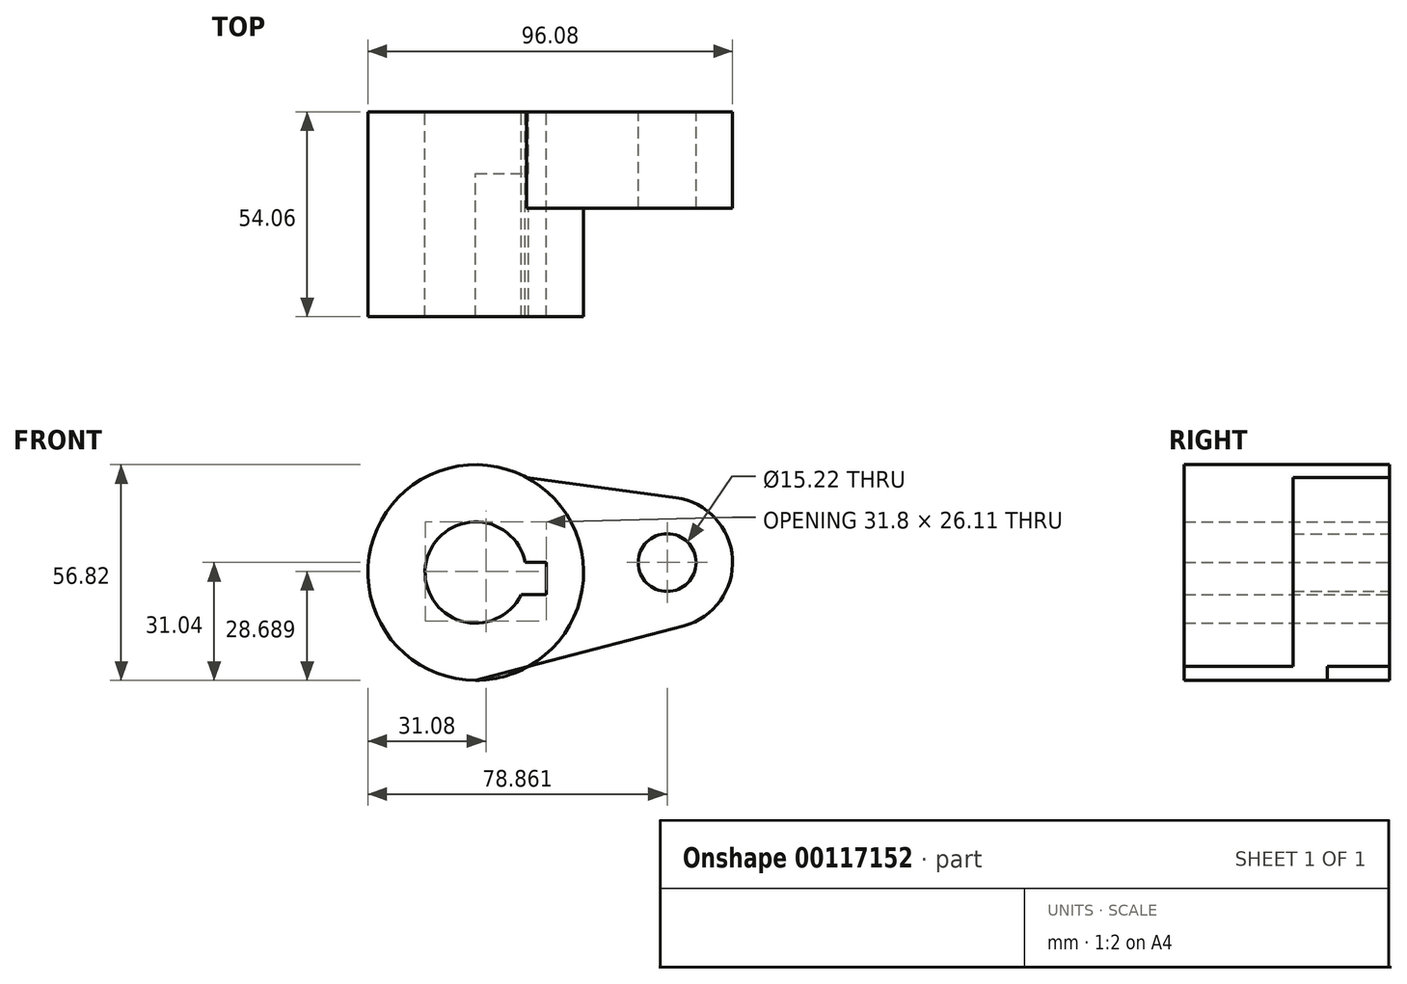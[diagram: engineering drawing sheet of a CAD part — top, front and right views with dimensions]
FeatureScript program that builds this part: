
annotation { "Feature Type Name" : "Feature", "Feature Type Description" : "" }
export const myFeature = defineFeature(function(context is Context, id is Id, definition is map)
    precondition{}
    {
        {
            var Q0;
            Q0=qCreatedBy(makeId("Front.planeOp"),FACE);
            var sketch = newSketch(context, id + "F0", { "sketchPlane" : qUnion([Q0])});
            skCircle(sketch, "E0", {"center": v(0, -2.63) * mm, "radius": 28.4 * mm});
            skCircle(sketch, "E1", {"center": v(50.45, 0) * mm, "radius": 17.22 * mm});
            skLineSegment(sketch, "E2", {"start": v(0, -31.04) * mm, "end": v(54.82, -16.66) * mm});
            skLineSegment(sketch, "E3", {"start": v(13.45, 22.4) * mm, "end": v(52.76, 17.07) * mm});
            skCircle(sketch, "E4", {"center": v(0, -2.63) * mm, "radius": 13.34 * mm});
            skCircle(sketch, "E5", {"center": v(50.45, 0) * mm, "radius": 7.6 * mm});
            skLineSegment(sketch, "E6.bottom", {"start": v(-17.95, 0) * mm, "end": v(18.57, 0) * mm});
            skLineSegment(sketch, "E6.top", {"start": v(-17.95, -8.51) * mm, "end": v(18.57, -8.51) * mm});
            skLineSegment(sketch, "E6.left", {"start": v(-17.95, 0) * mm, "end": v(-17.95, -8.51) * mm});
            skLineSegment(sketch, "E6.right", {"start": v(18.57, 0) * mm, "end": v(18.57, -8.51) * mm});
            skSolve(sketch);
        }
        {
            var Q0;
            {var subQ0=sQuery(id+"F0.wireOp",EDGE,"E6.left");Q0=makeQuery(id+"F0.imprint","IMPRINT",FACE,{"disambiguationData":[TD([[makeQuery(id+"F0.imprint","IMPRINT",EDGE,{"derivedFrom":subQ0}),-1.0]])]});}
            var Q1;
            {var subQ0=sQuery(id+"F0.wireOp",EDGE,"E3");Q1=makeQuery(id+"F0.imprint","IMPRINT",FACE,{"disambiguationData":[TD([[makeQuery(id+"F0.imprint","IMPRINT",EDGE,{"derivedFrom":subQ0}),-1.0]])]});}
            var Q2;
            Q2=makeQuery(id+"F0.imprint","IMPRINT",FACE,{"disambiguationData":[TD([[makeQuery(id+"F0.imprint","IMPRINT",EDGE,{"derivedFrom":sQuery(id+"F0.wireOp",EDGE,"E5")}),-1.0]])]});
            var Q3;
            {var subQ5=sQuery(id+"F0.wireOp",EDGE,"E6.left");Q3=makeQuery(id+"F0.imprint","IMPRINT",FACE,{"disambiguationData":[TD([[makeQuery(id+"F0.imprint","IMPRINT",EDGE,{"derivedFrom":subQ5}),1.0]])]});}
            extrude(context, id + "F1", {"entities" : qUnion([Q0, Q1, Q2, Q3]), "depth" : 25.4 * mm});
        }
        {
            var Q0;
            Q0 = qSketchRegion(id + "F0", true);
            extrude(context, id + "F2", {"entities" : qUnion([Q0]), "operationType" : NewBodyOperationType.ADD, "depth" : 16.33 * mm});
        }
        {
            var Q0;
            {var subQ5=sQuery(id+"F0.wireOp",EDGE,"E6.left");Q0=makeQuery(id+"F0.imprint","IMPRINT",FACE,{"disambiguationData":[TD([[makeQuery(id+"F0.imprint","IMPRINT",EDGE,{"derivedFrom":subQ5}),1.0]])]});}
            var Q1;
            {var subQ0=sQuery(id+"F0.wireOp",EDGE,"E6.left");Q1=makeQuery(id+"F0.imprint","IMPRINT",FACE,{"disambiguationData":[TD([[makeQuery(id+"F0.imprint","IMPRINT",EDGE,{"derivedFrom":subQ0}),-1.0]])]});}
            extrude(context, id + "F3", {"entities" : qUnion([Q0, Q1]), "operationType" : NewBodyOperationType.ADD, "depth" : 54.06 * mm});
        }
    });
